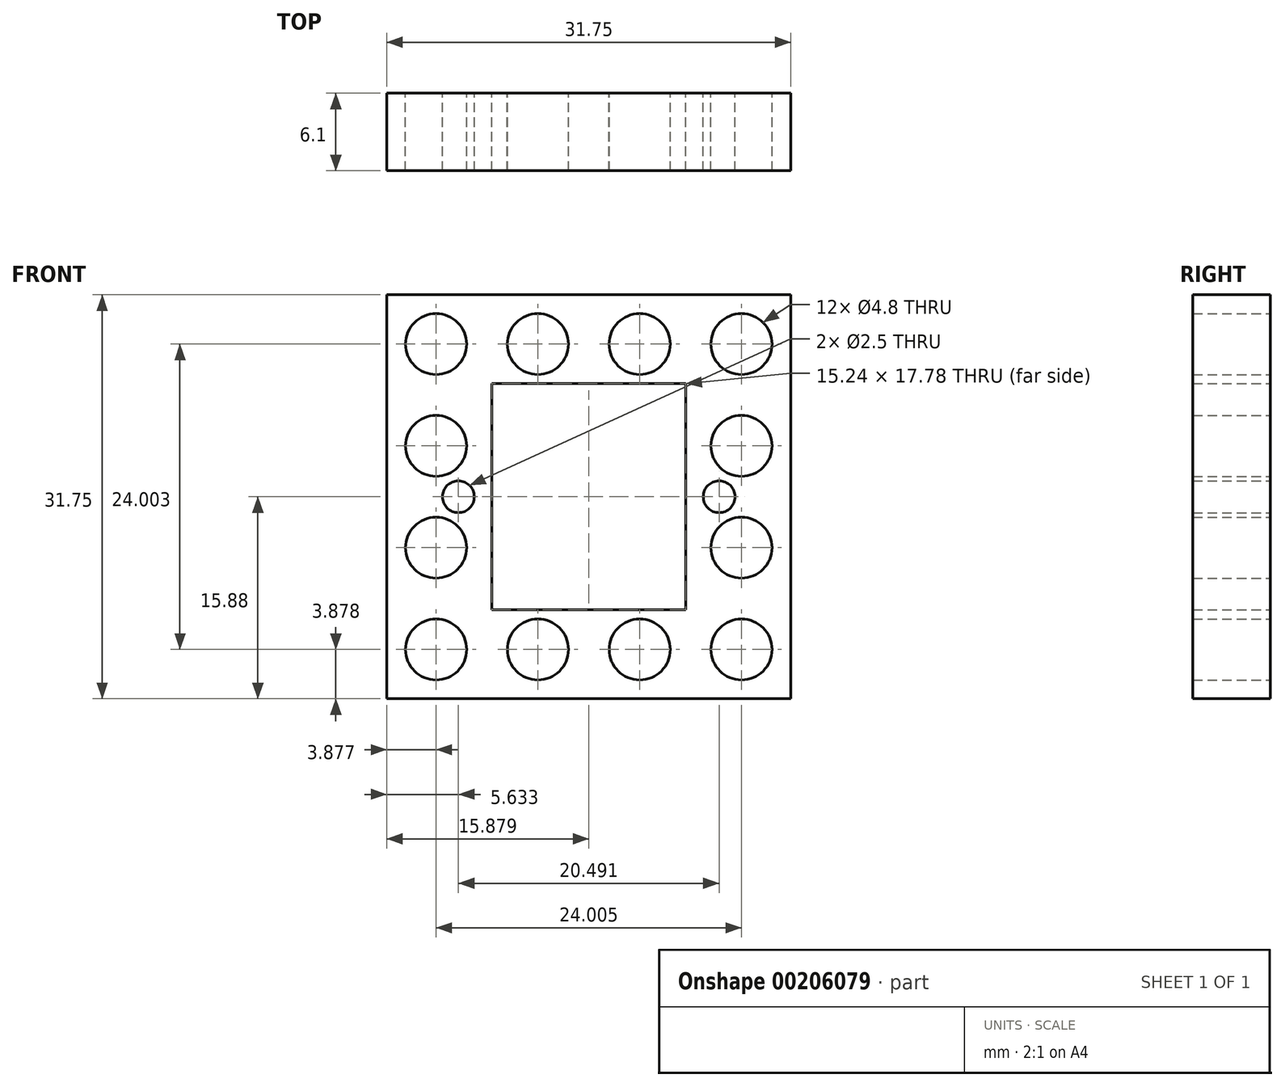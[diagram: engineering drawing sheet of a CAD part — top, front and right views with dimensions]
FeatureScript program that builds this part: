
annotation { "Feature Type Name" : "Feature", "Feature Type Description" : "" }
export const myFeature = defineFeature(function(context is Context, id is Id, definition is map)
    precondition{}
    {
        {
            var Q0;
            Q0=qCreatedBy(makeId("Front.planeOp"),FACE);
            var sketch = newSketch(context, id + "F0", { "sketchPlane" : qUnion([Q0])});
            skCircle(sketch, "E0", {"center": v(-9.07, -0.6) * mm, "radius": 1.25 * mm});
            skLineSegment(sketch, "E1.right", {"start": v(8.8, 8.29) * mm, "end": v(8.8, -9.5) * mm});
            skCircle(sketch, "E2", {"center": v(-10.82, 11.4) * mm, "radius": 2.4 * mm});
            skCircle(sketch, "E3.1.0.0", {"center": v(-2.82, 11.4) * mm, "radius": 2.4 * mm});
            skCircle(sketch, "E3.2.0.0", {"center": v(5.18, 11.4) * mm, "radius": 2.4 * mm});
            skLineSegment(sketch, "E3.direction1", {"start": v(-10.82, 11.4) * mm, "end": v(-2.82, 11.4) * mm, "construction": true});
            skCircle(sketch, "E4.0.3.0", {"center": v(13.18, 11.4) * mm, "radius": 2.4 * mm});
            skLineSegment(sketch, "E5.bottom", {"start": v(-14.7, 15.27) * mm, "end": v(17.05, 15.27) * mm});
            skLineSegment(sketch, "E5.top", {"start": v(-14.7, -16.48) * mm, "end": v(17.05, -16.48) * mm});
            skLineSegment(sketch, "E5.left", {"start": v(-14.7, 15.27) * mm, "end": v(-14.7, -16.48) * mm});
            skLineSegment(sketch, "E5.right", {"start": v(17.05, 15.27) * mm, "end": v(17.05, -16.48) * mm});
            skCircle(sketch, "E6.MirrorC", {"center": v(-10.82, -12.6) * mm, "radius": 2.4 * mm});
            skCircle(sketch, "E7.MirrorC", {"center": v(-2.82, -12.6) * mm, "radius": 2.4 * mm});
            skCircle(sketch, "E8.MirrorC", {"center": v(5.18, -12.6) * mm, "radius": 2.4 * mm});
            skCircle(sketch, "E9.MirrorC", {"center": v(13.18, -12.6) * mm, "radius": 2.4 * mm});
            skCircle(sketch, "E10.0.1.0", {"center": v(-10.82, 3.4) * mm, "radius": 2.4 * mm});
            skCircle(sketch, "E10.0.2.0", {"center": v(-10.82, -4.6) * mm, "radius": 2.4 * mm});
            skLineSegment(sketch, "E10.direction1", {"start": v(-10.82, 11.4) * mm, "end": v(-35.24, 11.4) * mm, "construction": true});
            skLineSegment(sketch, "E10.direction2", {"start": v(-10.82, 11.4) * mm, "end": v(-10.82, 3.4) * mm, "construction": true});
            skCircle(sketch, "E11.MirrorC", {"center": v(13.18, 3.4) * mm, "radius": 2.4 * mm});
            skCircle(sketch, "E12.MirrorC", {"center": v(13.18, -4.6) * mm, "radius": 2.4 * mm});
            skLineSegment(sketch, "E13", {"start": v(-6.44, -9.5) * mm, "end": v(8.8, -9.5) * mm});
            skLineSegment(sketch, "E14", {"start": v(8.8, 8.29) * mm, "end": v(-6.44, 8.29) * mm});
            skLineSegment(sketch, "E15", {"start": v(-6.44, 8.29) * mm, "end": v(-6.44, -9.5) * mm});
            skLineSegment(sketch, "E16", {"start": v(-6.44, -0.6) * mm, "end": v(8.8, -0.6) * mm});
            skLineSegment(sketch, "E17", {"start": v(1.18, 8.29) * mm, "end": v(1.18, -9.5) * mm});
            skCircle(sketch, "E18.MirrorC", {"center": v(11.42, -0.6) * mm, "radius": 1.25 * mm});
            skLineSegment(sketch, "E19", {"start": v(13.18, 11.4) * mm, "end": v(13.18, -12.6) * mm});
            skSolve(sketch);
        }
        {
            var Q0;
            Q0=makeQuery(id+"F0.imprint","IMPRINT",FACE,{"disambiguationData":[TD([[makeQuery(id+"F0.imprint","IMPRINT",EDGE,{"derivedFrom":sQuery(id+"F0.wireOp",EDGE,"E0")}),-1.0]])]});
            extrude(context, id + "F1", {"entities" : qUnion([Q0]), "depth" : 6.1 * mm, "offsetDistance" : 25.4 * mm});
        }
    });
